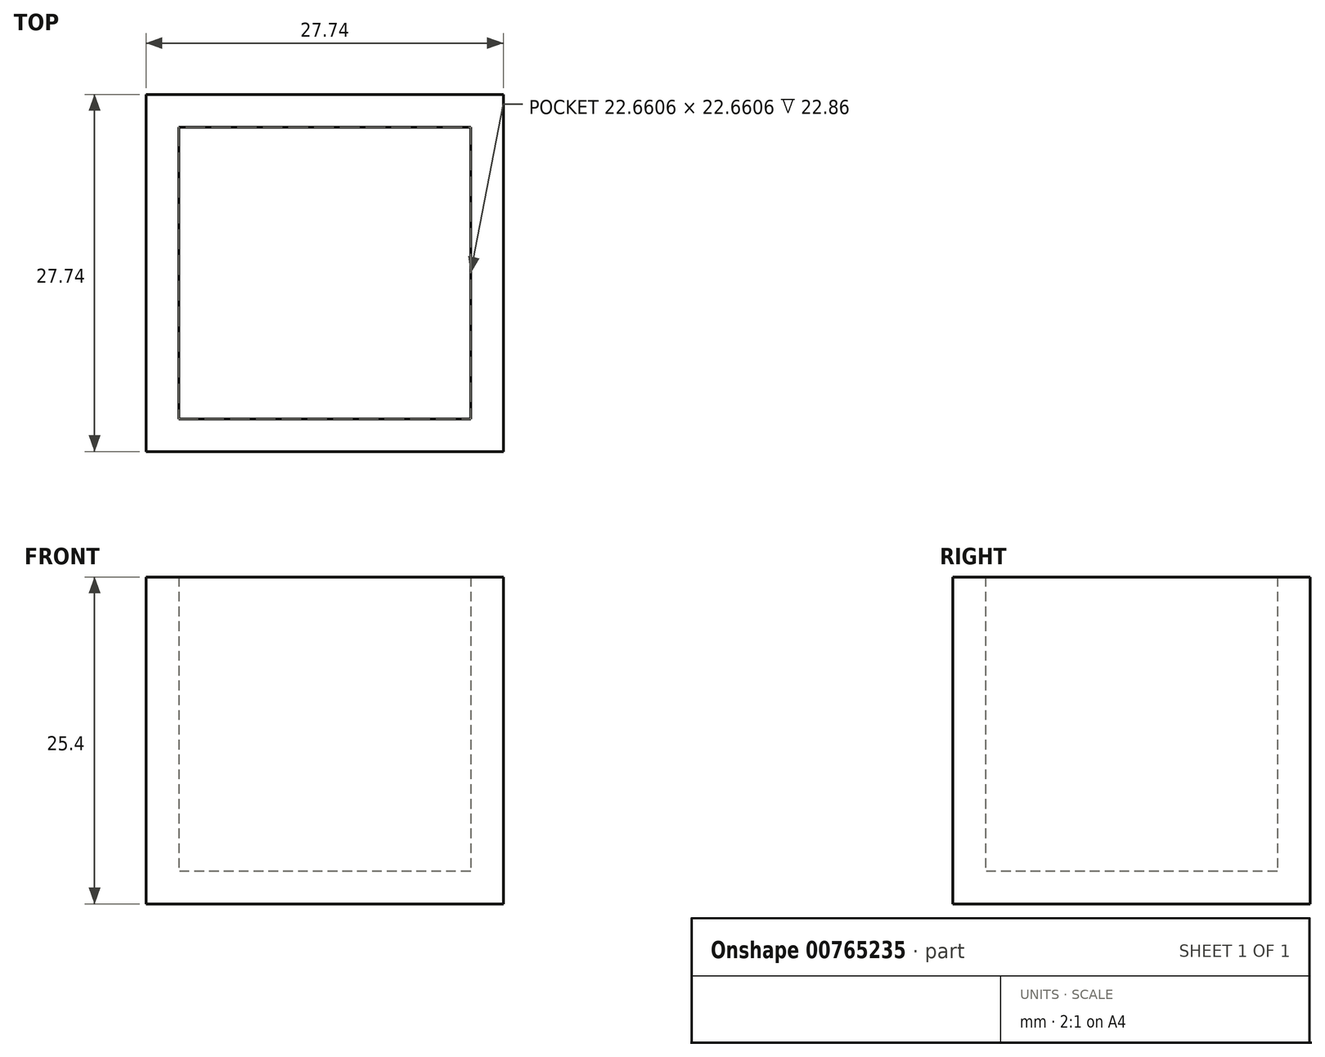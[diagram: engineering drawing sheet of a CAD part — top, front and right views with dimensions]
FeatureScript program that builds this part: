
annotation { "Feature Type Name" : "Feature", "Feature Type Description" : "" }
export const myFeature = defineFeature(function(context is Context, id is Id, definition is map)
    precondition{}
    {
        {
            var Q0;
            Q0=qCreatedBy(makeId("Top.planeOp"),FACE);
            var sketch = newSketch(context, id + "F0", { "sketchPlane" : qUnion([Q0])});
            skLineSegment(sketch, "E0.bottom", {"start": v(13.87, 13.87) * mm, "end": v(-13.87, 13.87) * mm});
            skLineSegment(sketch, "E0.top", {"start": v(13.87, -13.87) * mm, "end": v(-13.87, -13.87) * mm});
            skLineSegment(sketch, "E0.left", {"start": v(13.87, 13.87) * mm, "end": v(13.87, -13.87) * mm});
            skLineSegment(sketch, "E0.right", {"start": v(-13.87, 13.87) * mm, "end": v(-13.87, -13.87) * mm});
            skPoint(sketch, "E0.middle", {"position": v(0, 0) * mm});
            skSolve(sketch);
        }
        {
            var Q0;
            Q0=qCreatedBy(makeId("Top.planeOp"),FACE);
            var sketch = newSketch(context, id + "F1", { "sketchPlane" : qUnion([Q0])});
            skSolve(sketch);
        }
        {
            var Q0;
            Q0 = qSketchRegion(id + "F1", true);
            var Q1;
            Q1=makeQuery(id+"F0.imprint","IMPRINT",FACE,{"disambiguationData":[TD([[makeQuery(id+"F0.imprint","IMPRINT",EDGE,{"derivedFrom":sQuery(id+"F0.wireOp",EDGE,"E0.bottom")}),1.0]])]});
            extrude(context, id + "F2", {"entities" : qUnion([Q0, Q1]), "depth" : 25.4 * mm, "offsetDistance" : 25.4 * mm});
        }
        {
            var Q0;
            Q0=makeQuery(id+"F2.opExtrude","CAP_FACE",FACE,{"disambiguationData":[OSD([sQuery(id+"F0.wireOp",EDGE,"E0.bottom"),sQuery(id+"F0.wireOp",EDGE,"E0.top"),sQuery(id+"F0.wireOp",EDGE,"E0.left"),sQuery(id+"F0.wireOp",EDGE,"E0.right")])],"isStart":false});
            shell(context, id + "F3", {"entities" : qUnion([Q0]), "thickness" : 2.54 * mm});
        }
    });
